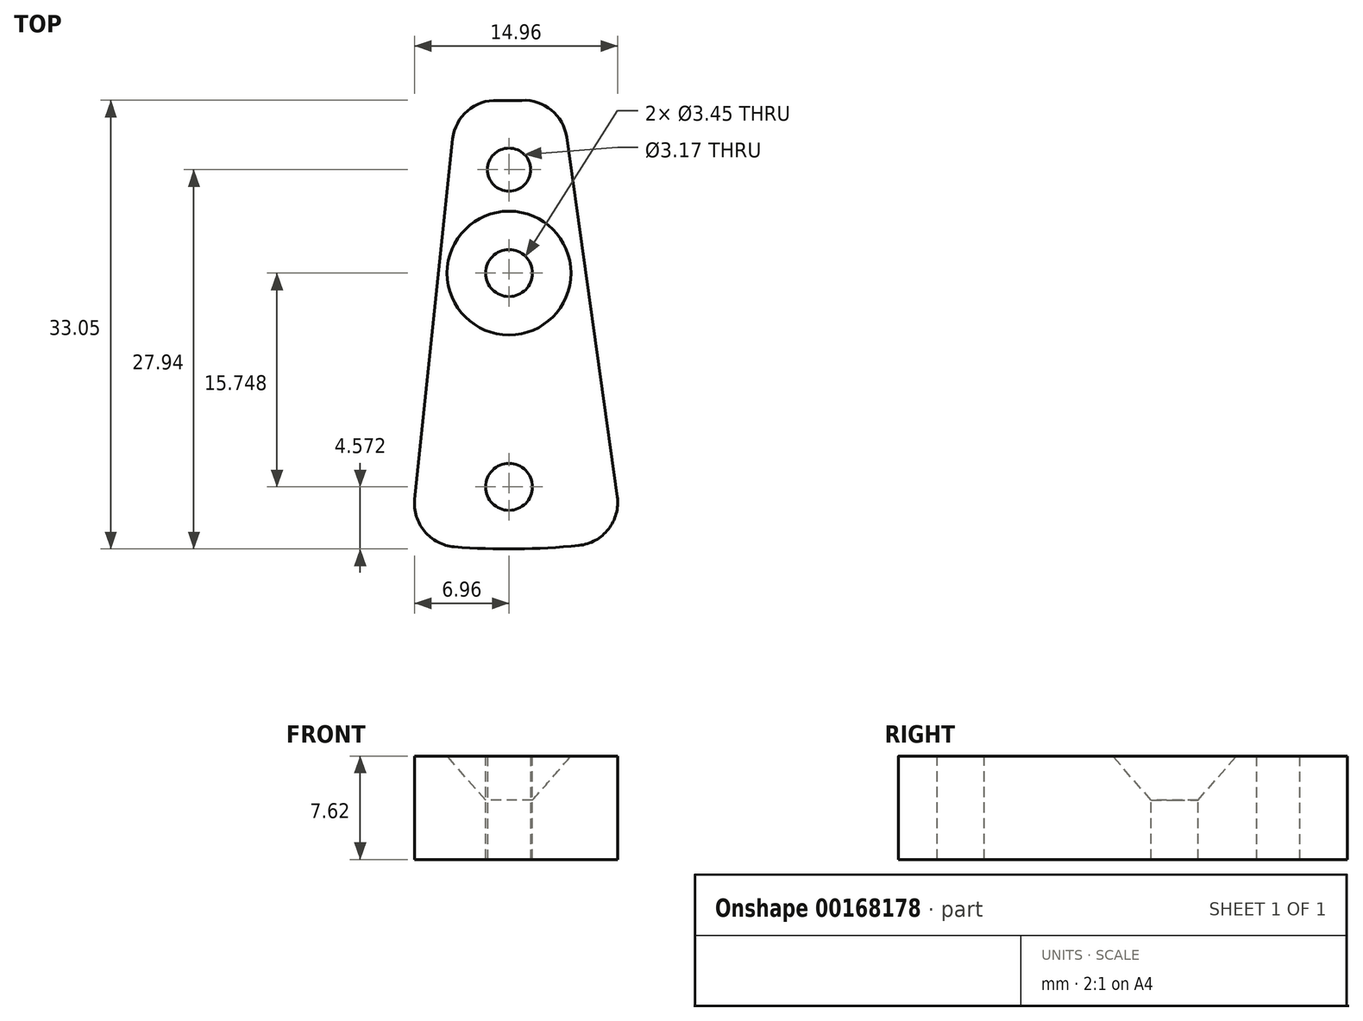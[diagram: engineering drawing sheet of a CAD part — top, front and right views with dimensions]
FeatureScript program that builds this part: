
annotation { "Feature Type Name" : "Feature", "Feature Type Description" : "" }
export const myFeature = defineFeature(function(context is Context, id is Id, definition is map)
    precondition{}
    {
        {
            var Q0;
            Q0=qCreatedBy(makeId("Top.planeOp"),FACE);
            var sketch = newSketch(context, id + "F0", { "sketchPlane" : qUnion([Q0])});
            skArc(sketch, "E0", {"start": v(3.81, -17.37) * mm, "mid": v(0, -17.78) * mm, "end": v(-3.81, -17.37) * mm});
            skArc(sketch, "E1", {"start": v(8.41, -50.1) * mm, "mid": v(0.58, -50.8) * mm, "end": v(-7.27, -50.28) * mm});
            skLineSegment(sketch, "E2", {"start": v(-3.81, -17.37) * mm, "end": v(3.81, -17.37) * mm, "construction": true});
            skLineSegment(sketch, "E3", {"start": v(0, 0) * mm, "end": v(-3.81, -17.37) * mm, "construction": true});
            skLineSegment(sketch, "E4", {"start": v(0, 0) * mm, "end": v(3.81, -17.37) * mm, "construction": true});
            skLineSegment(sketch, "E5", {"start": v(-3.81, -17.37) * mm, "end": v(-7.27, -50.28) * mm});
            skLineSegment(sketch, "E6", {"start": v(3.81, -17.37) * mm, "end": v(8.41, -50.1) * mm});
            skPoint(sketch, "E7", {"position": v(0, -17.37) * mm});
            skSolve(sketch);
        }
        {
            var Q0;
            Q0=qSketchRegion(id+"F0",true);
            extrude(context, id + "F1", {"entities" : qUnion([Q0]), "depth" : 7.62 * mm});
        }
        {
            var Q0;
            Q0=makeQuery(id+"F1.opExtrude","SWEPT_EDGE",EDGE,{"disambiguationData":[OSD([sQuery(id+"F0.wireOp",EDGE,"E1"),sQuery(id+"F0.wireOp",EDGE,"E5")])]});
            var Q1;
            Q1=makeQuery(id+"F1.opExtrude","SWEPT_EDGE",EDGE,{"disambiguationData":[OSD([sQuery(id+"F0.wireOp",EDGE,"E0"),sQuery(id+"F0.wireOp",EDGE,"E5")])]});
            var Q2;
            Q2=makeQuery(id+"F1.opExtrude","SWEPT_EDGE",EDGE,{"disambiguationData":[OSD([sQuery(id+"F0.wireOp",EDGE,"E1"),sQuery(id+"F0.wireOp",EDGE,"E6")])]});
            var Q3;
            Q3=makeQuery(id+"F1.opExtrude","SWEPT_EDGE",EDGE,{"disambiguationData":[OSD([sQuery(id+"F0.wireOp",EDGE,"E0"),sQuery(id+"F0.wireOp",EDGE,"E6")])]});
            fillet(context, id + "F2", {"entities" : qUnion([Q0, Q1, Q2, Q3]), "radius" : 3.17 * mm, "tangentPropagation" : true, "allowEdgeOverflow" : false});
        }
        {
            var Q0;
            Q0=makeQuery(id+"F1.opExtrude","CAP_FACE",FACE,{"disambiguationData":[OSD([sQuery(id+"F0.wireOp",EDGE,"E0"),sQuery(id+"F0.wireOp",EDGE,"E1"),sQuery(id+"F0.wireOp",EDGE,"E5"),sQuery(id+"F0.wireOp",EDGE,"E6")])],"isStart":false});
            var sketch = newSketch(context, id + "F3", { "sketchPlane" : qUnion([Q0])});
            skPoint(sketch, "E8", {"position": v(0, -46.23) * mm});
            skSolve(sketch);
        }
        {
            var Q0;
            Q0=sQuery(id+"F3.wireOp",VERTEX,"E8");
            var Q1;
            Q1=makeQuery(id+"F1.opExtrude","SWEPT_BODY",BODY,{"disambiguationData":[OSD([sQuery(id+"F0.wireOp",EDGE,"E0"),sQuery(id+"F0.wireOp",EDGE,"E1"),sQuery(id+"F0.wireOp",EDGE,"E5"),sQuery(id+"F0.wireOp",EDGE,"E6")])]});
            hole(context, id + "F4", {"style" : HoleStyle.SIMPLE, "endStyle" : HoleEndStyle.THROUGH, "standardTappedOrClearance" : lookupTablePath({ "standard" : "ANSI", "engagement" : "75%", "pitch" : "32 tpi", "size" : "#8", "type" : "Tapped" }), "standardBlindInLast" : lookupTablePath({ "standard" : "ANSI", "engagement" : "75%", "pitch" : "32 tpi", "size" : "#8", "type" : "Tapped" }), "holeDiameter" : 3.45 * mm, "locations" : qUnion([Q0]), "scope" : qUnion([Q1]), "isTappedThrough" : true, "majorDiameter" : 4.17 * mm, "showTappedDepth" : true});
        }
        {
            var Q0;
            Q0=makeQuery(id+"F1.opExtrude","CAP_FACE",FACE,{"disambiguationData":[OSD([sQuery(id+"F0.wireOp",EDGE,"E0"),sQuery(id+"F0.wireOp",EDGE,"E1"),sQuery(id+"F0.wireOp",EDGE,"E5"),sQuery(id+"F0.wireOp",EDGE,"E6")])],"isStart":false});
            var sketch = newSketch(context, id + "F5", { "sketchPlane" : qUnion([Q0])});
            skPoint(sketch, "E9", {"position": v(0, -30.48) * mm});
            skSolve(sketch);
        }
        {
            var Q0;
            Q0=sQuery(id+"F5.wireOp",VERTEX,"E9");
            var Q1;
            Q1=makeQuery(id+"F1.opExtrude","SWEPT_BODY",BODY,{"disambiguationData":[OSD([sQuery(id+"F0.wireOp",EDGE,"E0"),sQuery(id+"F0.wireOp",EDGE,"E1"),sQuery(id+"F0.wireOp",EDGE,"E5"),sQuery(id+"F0.wireOp",EDGE,"E6")])]});
            hole(context, id + "F6", {"style" : HoleStyle.C_SINK, "endStyle" : HoleEndStyle.THROUGH, "standardTappedOrClearance" : lookupTablePath({ "standard" : "ANSI", "engagement" : "75%", "pitch" : "32 tpi", "size" : "#8", "type" : "Tapped" }), "standardBlindInLast" : lookupTablePath({ "standard" : "ANSI", "engagement" : "75%", "pitch" : "32 tpi", "size" : "#8", "type" : "Tapped" }), "holeDiameter" : 3.45 * mm, "cSinkDiameter" : 9.12 * mm, "cSinkAngle" : 82 * degree, "locations" : qUnion([Q0]), "scope" : qUnion([Q1]), "isTappedThrough" : true, "majorDiameter" : 4.17 * mm, "showTappedDepth" : true});
        }
        {
            var Q0;
            Q0=makeQuery(id+"F1.opExtrude","CAP_FACE",FACE,{"disambiguationData":[OSD([sQuery(id+"F0.wireOp",EDGE,"E0"),sQuery(id+"F0.wireOp",EDGE,"E1"),sQuery(id+"F0.wireOp",EDGE,"E5"),sQuery(id+"F0.wireOp",EDGE,"E6")])],"isStart":true});
            var sketch = newSketch(context, id + "F7", { "sketchPlane" : qUnion([Q0])});
            skCircle(sketch, "E10", {"center": v(0, 22.86) * mm, "radius": 1.59 * mm});
            skSolve(sketch);
        }
        {
            var Q0;
            Q0=qSketchRegion(id+"F7",true);
            extrude(context, id + "F8", {"entities" : qUnion([Q0]), "operationType" : NewBodyOperationType.REMOVE, "endBound" : BoundingType.THROUGH_ALL, "oppositeDirection" : true, "depth" : 25.4 * mm});
        }
    });
